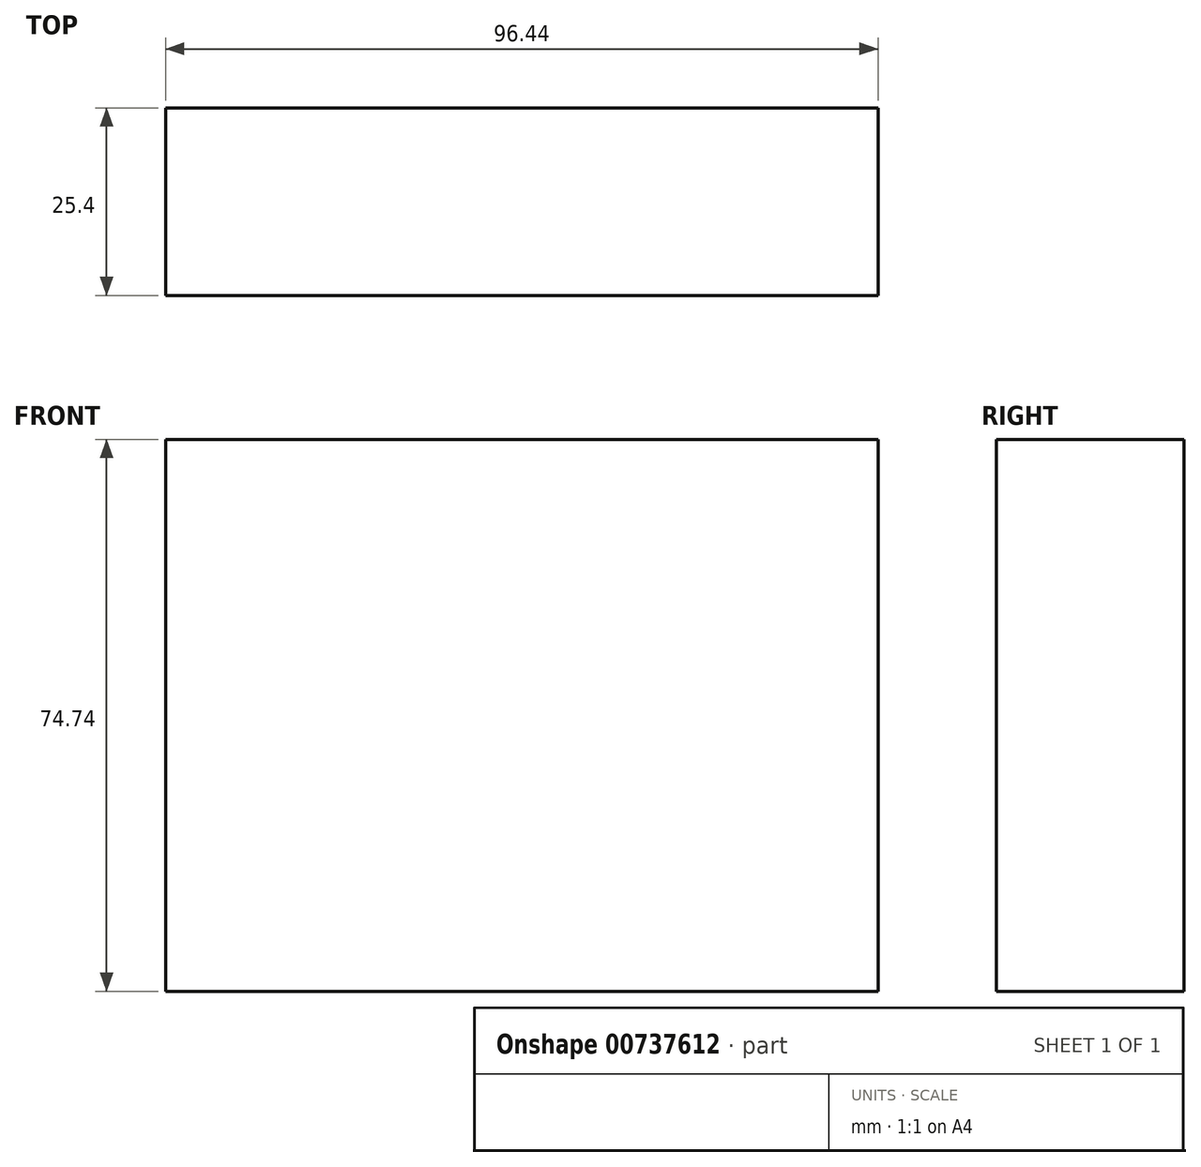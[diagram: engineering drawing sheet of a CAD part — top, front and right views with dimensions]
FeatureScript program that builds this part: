
annotation { "Feature Type Name" : "Feature", "Feature Type Description" : "" }
export const myFeature = defineFeature(function(context is Context, id is Id, definition is map)
    precondition{}
    {
        {
            var Q0;
            Q0=qCreatedBy(makeId("Front.planeOp"),FACE);
            var sketch = newSketch(context, id + "F0", { "sketchPlane" : qUnion([Q0])});
            skLineSegment(sketch, "E0.bottom", {"start": v(-48.22, 37.37) * mm, "end": v(48.22, 37.37) * mm});
            skLineSegment(sketch, "E0.top", {"start": v(-48.22, -37.37) * mm, "end": v(48.22, -37.37) * mm});
            skLineSegment(sketch, "E0.left", {"start": v(-48.22, 37.37) * mm, "end": v(-48.22, -37.37) * mm});
            skLineSegment(sketch, "E0.right", {"start": v(48.22, 37.37) * mm, "end": v(48.22, -37.37) * mm});
            skPoint(sketch, "E0.middle", {"position": v(0, 0) * mm});
            skSolve(sketch);
        }
        {
            var Q0;
            Q0=makeQuery(id+"F0.imprint","IMPRINT",FACE,{"disambiguationData":[TD([[makeQuery(id+"F0.imprint","IMPRINT",EDGE,{"derivedFrom":sQuery(id+"F0.wireOp",EDGE,"E0.bottom")}),-1.0]])]});
            extrude(context, id + "F1", {"entities" : qUnion([Q0]), "depth" : 25.4 * mm, "offsetDistance" : 25.4 * mm});
        }
    });
